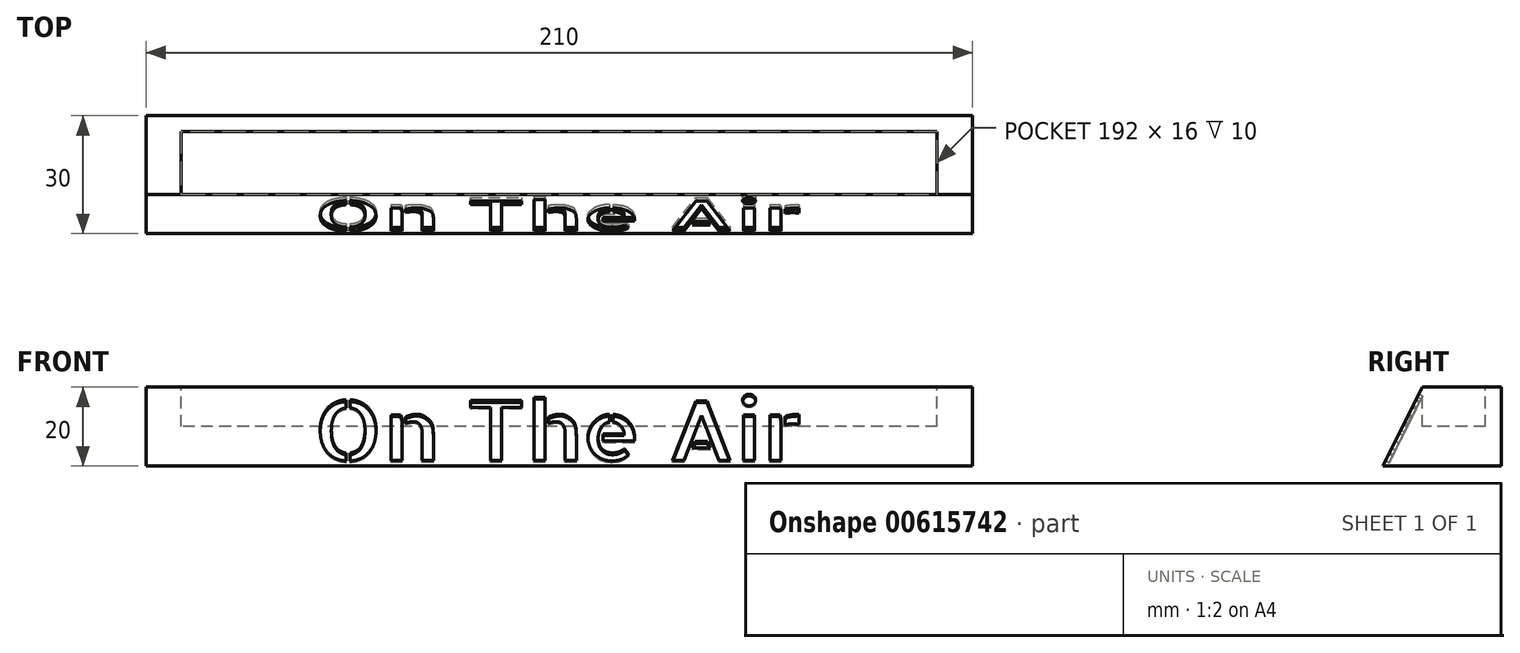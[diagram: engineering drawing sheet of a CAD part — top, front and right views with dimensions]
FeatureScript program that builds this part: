
annotation { "Feature Type Name" : "Feature", "Feature Type Description" : "" }
export const myFeature = defineFeature(function(context is Context, id is Id, definition is map)
    precondition{}
    {
        {
            var Q0;
            Q0=qCreatedBy(makeId("Top.planeOp"),FACE);
            var sketch = newSketch(context, id + "F0", { "sketchPlane" : qUnion([Q0])});
            skLineSegment(sketch, "E0.bottom", {"start": v(105, -10) * mm, "end": v(-105, -10) * mm});
            skLineSegment(sketch, "E0.top", {"start": v(105, 10) * mm, "end": v(-105, 10) * mm});
            skLineSegment(sketch, "E0.left", {"start": v(105, -10) * mm, "end": v(105, 10) * mm});
            skLineSegment(sketch, "E0.right", {"start": v(-105, -10) * mm, "end": v(-105, 10) * mm});
            skPoint(sketch, "E0.middle", {"position": v(0, 0) * mm});
            skSolve(sketch);
        }
        {
            var Q0;
            Q0 = qSketchRegion(id + "F0", true);
            extrude(context, id + "F1", {"entities" : qUnion([Q0]), "depth" : 20 * mm, "offsetDistance" : 25 * mm});
        }
        {
            var Q0;
            Q0=makeQuery(id+"F1.opExtrude","SWEPT_FACE",FACE,{"disambiguationData":[OSD([sQuery(id+"F0.wireOp",EDGE,"E0.right")])]});
            var sketch = newSketch(context, id + "F2", { "sketchPlane" : qUnion([Q0])});
            skLineSegment(sketch, "E1", {"start": v(10, 20) * mm, "end": v(20, 0) * mm});
            skLineSegment(sketch, "E2", {"start": v(20, 0) * mm, "end": v(10, 0) * mm});
            skSolve(sketch);
        }
        {
            var Q0;
            Q0=makeQuery(id+"F2.imprint","IMPRINT",FACE,{"disambiguationData":[TD([[makeQuery(id+"F2.imprint","IMPRINT",EDGE,{"derivedFrom":sQuery(id+"F2.wireOp",EDGE,"E1")}),-1.0]])]});
            extrude(context, id + "F3", {"entities" : qUnion([Q0]), "operationType" : NewBodyOperationType.ADD, "depth" : 0 * mm, "offsetDistance" : 25 * mm, "hasSecondDirection" : true, "secondDirectionOppositeDirection" : true, "secondDirectionDepth" : 210 * mm});
        }
        {
            var Q0;
            Q0=makeQuery(id+"F1.opExtrude","CAP_FACE",FACE,{"disambiguationData":[OSD([sQuery(id+"F0.wireOp",EDGE,"E0.bottom"),sQuery(id+"F0.wireOp",EDGE,"E0.top"),sQuery(id+"F0.wireOp",EDGE,"E0.left"),sQuery(id+"F0.wireOp",EDGE,"E0.right")])],"isStart":false});
            var sketch = newSketch(context, id + "F4", { "sketchPlane" : qUnion([Q0])});
            skLineSegment(sketch, "E3.bottom", {"start": v(-96, 6) * mm, "end": v(96, 6) * mm});
            skLineSegment(sketch, "E3.top", {"start": v(-96, -10) * mm, "end": v(96, -10) * mm});
            skLineSegment(sketch, "E3.left", {"start": v(-96, 6) * mm, "end": v(-96, -10) * mm});
            skLineSegment(sketch, "E3.right", {"start": v(96, 6) * mm, "end": v(96, -10) * mm});
            skSolve(sketch);
        }
        {
            var Q0;
            Q0=makeQuery(id+"F4.imprint","IMPRINT",FACE,{"disambiguationData":[TD([[makeQuery(id+"F4.imprint","IMPRINT",EDGE,{"derivedFrom":sQuery(id+"F4.wireOp",EDGE,"E3.bottom")}),-1.0]])]});
            extrude(context, id + "F5", {"entities" : qUnion([Q0]), "operationType" : NewBodyOperationType.REMOVE, "oppositeDirection" : true, "depth" : 10 * mm, "offsetDistance" : 25 * mm});
        }
        {
            var Q0;
            Q0=makeQuery(id+"F3.opExtrude","SWEPT_FACE",FACE,{"disambiguationData":[OSD([sQuery(id+"F2.wireOp",EDGE,"E1")])]});
            var sketch = newSketch(context, id + "F6", { "sketchPlane" : qUnion([Q0])});
            skText(sketch, "E4", { "text": "On The Air", "fontName": "AllertaStencil-Regular.ttf"});
            const initialGuessF6  = {"E4": [-0.0625, -0.00744, 1, 0, 0.01704]};
            skSetInitialGuess(sketch, initialGuessF6);
            skSolve(sketch);
        }
        {
            var Q0;
            Q0 = qSketchRegion(id + "F6", true);
            extrude(context, id + "F7", {"entities" : qUnion([Q0]), "operationType" : NewBodyOperationType.REMOVE, "oppositeDirection" : true, "depth" : 1 * mm, "offsetDistance" : 25 * mm});
        }
    });
